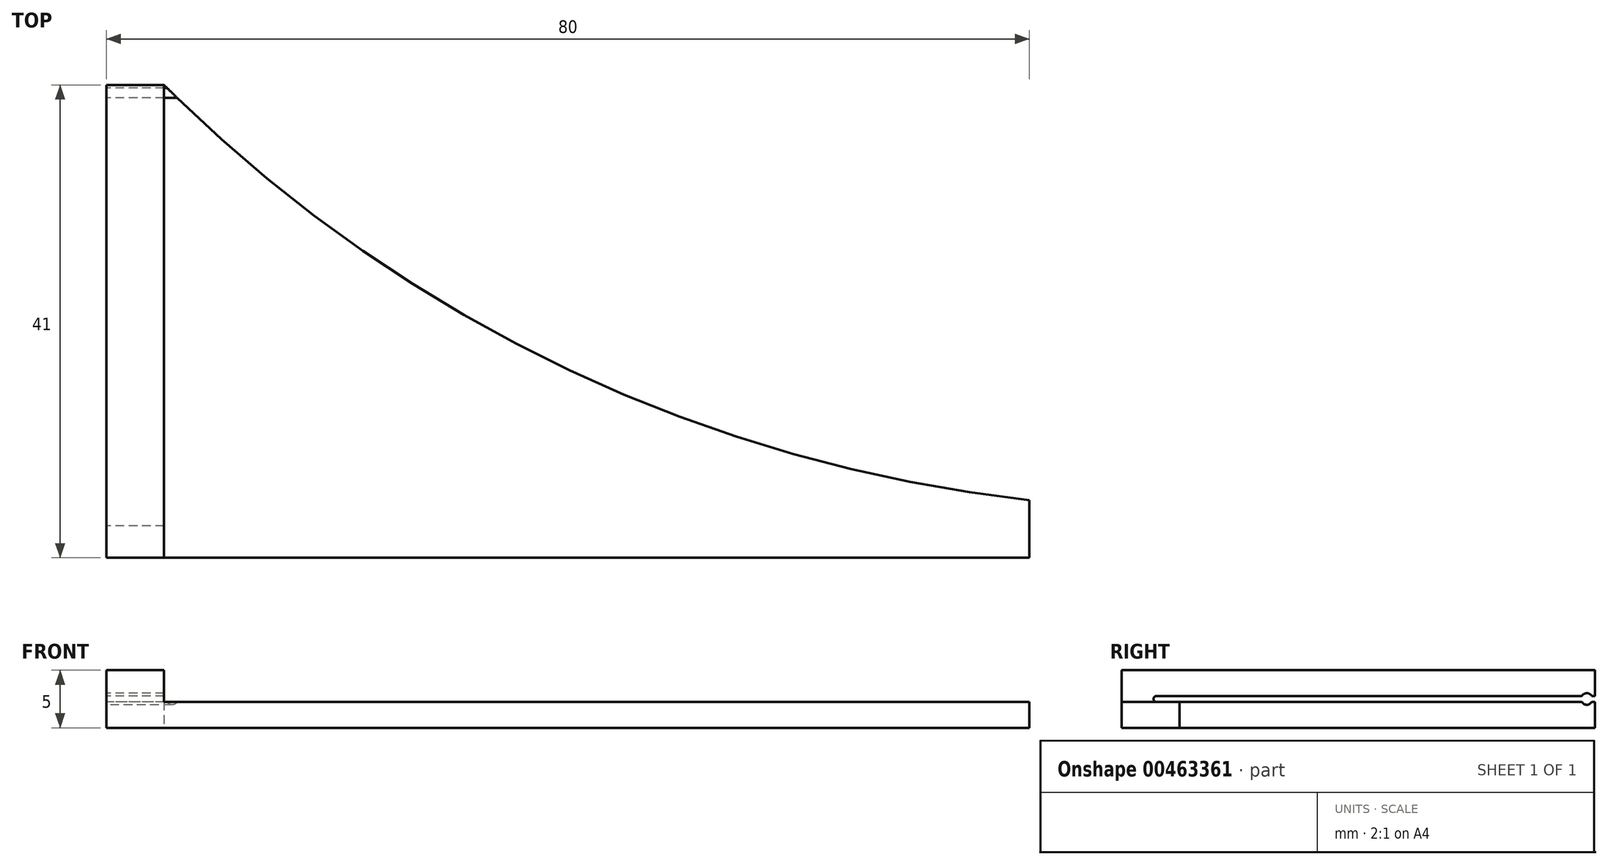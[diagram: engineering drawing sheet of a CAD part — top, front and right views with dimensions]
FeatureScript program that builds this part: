
annotation { "Feature Type Name" : "Feature", "Feature Type Description" : "" }
export const myFeature = defineFeature(function(context is Context, id is Id, definition is map)
    precondition{}
    {
        {
            var Q0;
            Q0=qCreatedBy(makeId("Top.planeOp"),FACE);
            var sketch = newSketch(context, id + "F0", { "sketchPlane" : qUnion([Q0])});
            skLineSegment(sketch, "E0", {"start": v(0, 0) * mm, "end": v(0, 41) * mm});
            skLineSegment(sketch, "E1", {"start": v(0, 0) * mm, "end": v(80, 0) * mm});
            skLineSegment(sketch, "E2", {"start": v(80, 0) * mm, "end": v(80, 5) * mm});
            skLineSegment(sketch, "E3", {"start": v(0, 41) * mm, "end": v(5, 41) * mm});
            skArc(sketch, "E4", {"start": v(5, 41) * mm, "mid": v(39.43, 16.6) * mm, "end": v(80, 5) * mm});
            skSolve(sketch);
        }
        {
            var Q0;
            Q0 = qSketchRegion(id + "F0", true);
            extrude(context, id + "F1", {"entities" : qUnion([Q0]), "depth" : 5 * mm});
        }
        {
            var Q0;
            Q0=makeQuery(id+"F1.opExtrude","SWEPT_FACE",FACE,{"disambiguationData":[OSD([sQuery(id+"F0.wireOp",EDGE,"E0")])]});
            var sketch = newSketch(context, id + "F2", { "sketchPlane" : qUnion([Q0])});
            skLineSegment(sketch, "E5", {"start": v(-41, 2.25) * mm, "end": v(-3, 2.25) * mm});
            skLineSegment(sketch, "E6", {"start": v(-41, 2.25) * mm, "end": v(-41, 2.75) * mm});
            skLineSegment(sketch, "E7", {"start": v(-41, 2.75) * mm, "end": v(-3, 2.75) * mm});
            skArc(sketch, "E8", {"start": v(-3, 2.25) * mm, "mid": v(-2.75, 2.5) * mm, "end": v(-3, 2.75) * mm});
            skSolve(sketch);
        }
        {
            var Q0;
            Q0 = qSketchRegion(id + "F2", true);
            extrude(context, id + "F3", {"entities" : qUnion([Q0]), "operationType" : NewBodyOperationType.REMOVE, "oppositeDirection" : true, "depth" : 1000 * mm});
        }
        {
            var Q0;
            Q0=makeQuery(id+"F1.opExtrude","SWEPT_FACE",FACE,{"disambiguationData":[OSD([sQuery(id+"F0.wireOp",EDGE,"E0")])]});
            var sketch = newSketch(context, id + "F4", { "sketchPlane" : qUnion([Q0])});
            skCircle(sketch, "E9", {"center": v(-40.3, 2.5) * mm, "radius": 0.5 * mm});
            skSolve(sketch);
        }
        {
            var Q0;
            Q0 = qSketchRegion(id + "F4", true);
            extrude(context, id + "F5", {"entities" : qUnion([Q0]), "operationType" : NewBodyOperationType.REMOVE, "oppositeDirection" : true, "depth" : 25 * mm});
        }
        {
            var Q0;
            Q0=makeQuery(id+"F1.opExtrude","CAP_FACE",FACE,{"disambiguationData":[OSD([sQuery(id+"F0.wireOp",EDGE,"E0"),sQuery(id+"F0.wireOp",EDGE,"E1"),sQuery(id+"F0.wireOp",EDGE,"E2"),sQuery(id+"F0.wireOp",EDGE,"E3"),sQuery(id+"F0.wireOp",EDGE,"E4")])],"isStart":false});
            var sketch = newSketch(context, id + "F6", { "sketchPlane" : qUnion([Q0])});
            skLineSegment(sketch, "E10.bottom", {"start": v(5, 41) * mm, "end": v(80, 41) * mm});
            skLineSegment(sketch, "E10.top", {"start": v(5, 0) * mm, "end": v(80, 0) * mm});
            skLineSegment(sketch, "E10.left", {"start": v(5, 41) * mm, "end": v(5, 0) * mm});
            skLineSegment(sketch, "E10.right", {"start": v(80, 41) * mm, "end": v(80, 0) * mm});
            skSolve(sketch);
        }
        {
            var Q0;
            Q0 = qSketchRegion(id + "F6", true);
            extrude(context, id + "F7", {"entities" : qUnion([Q0]), "operationType" : NewBodyOperationType.REMOVE, "oppositeDirection" : true, "depth" : 2.75 * mm});
        }
    });
